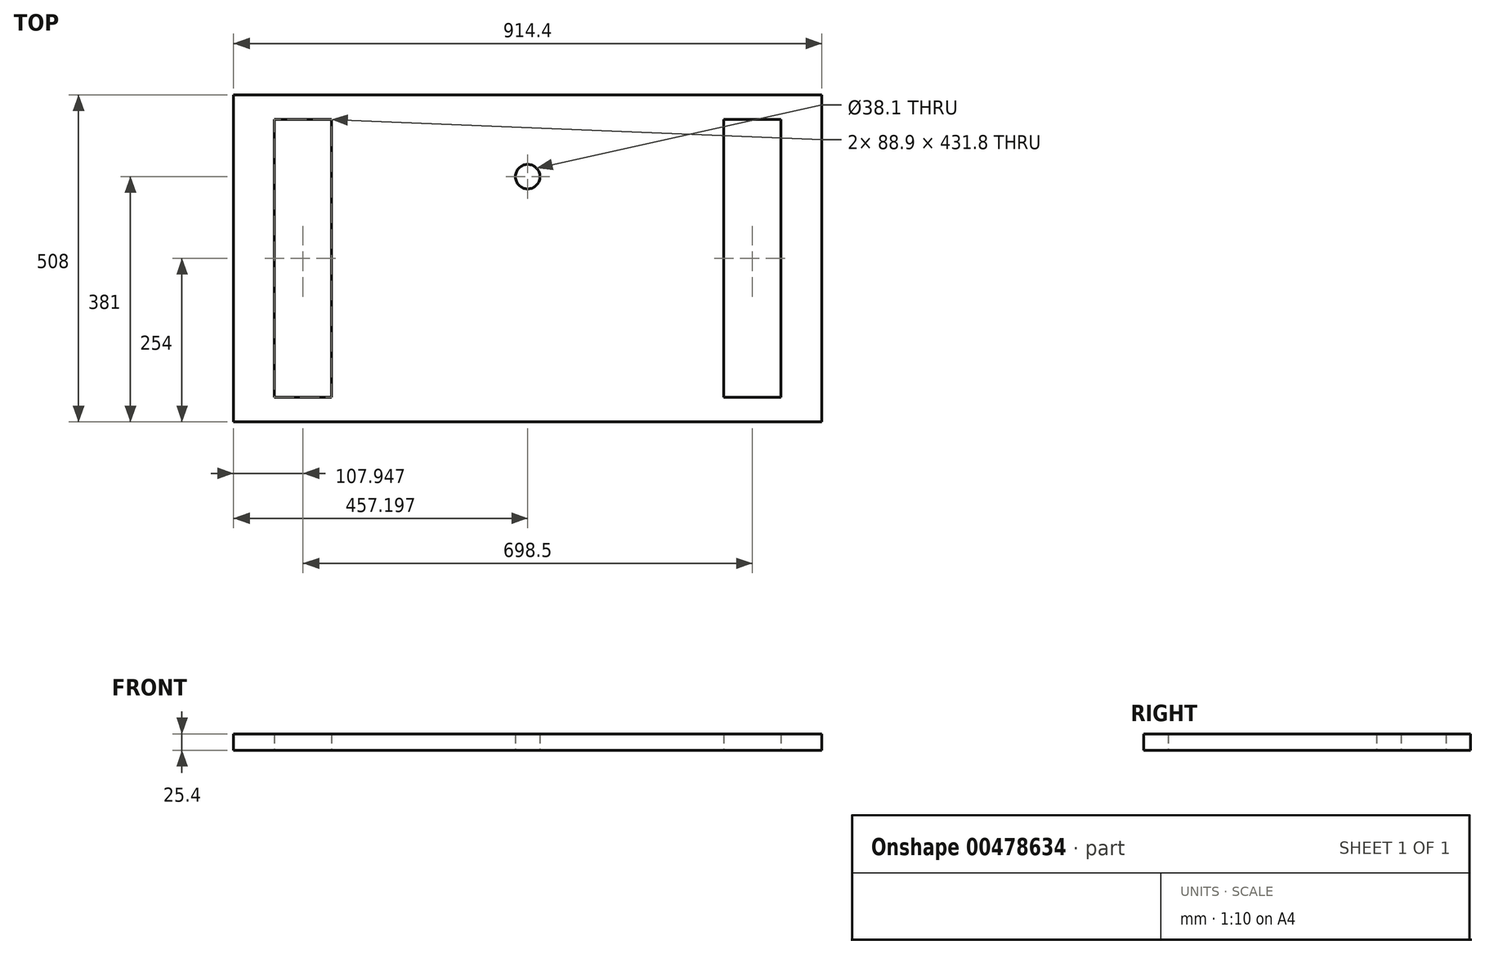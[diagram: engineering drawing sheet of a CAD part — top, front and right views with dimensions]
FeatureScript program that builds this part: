
annotation { "Feature Type Name" : "Feature", "Feature Type Description" : "" }
export const myFeature = defineFeature(function(context is Context, id is Id, definition is map)
    precondition{}
    {
        {
            var Q0;
            Q0=qCreatedBy(makeId("Top.planeOp"),FACE);
            var sketch = newSketch(context, id + "F0", { "sketchPlane" : qUnion([Q0])});
            skLineSegment(sketch, "E0.bottom", {"start": v(-444.73, 136.84) * mm, "end": v(469.67, 136.84) * mm});
            skLineSegment(sketch, "E0.top", {"start": v(-444.73, -371.16) * mm, "end": v(469.67, -371.16) * mm});
            skLineSegment(sketch, "E0.left", {"start": v(-444.73, 136.84) * mm, "end": v(-444.73, -371.16) * mm});
            skLineSegment(sketch, "E0.right", {"start": v(469.67, 136.84) * mm, "end": v(469.67, -371.16) * mm});
            skLineSegment(sketch, "E1", {"start": v(12.47, 136.84) * mm, "end": v(12.47, -371.16) * mm, "construction": true});
            skLineSegment(sketch, "E2.bottom", {"start": v(-381.23, 98.74) * mm, "end": v(-292.33, 98.74) * mm});
            skLineSegment(sketch, "E2.top", {"start": v(-381.23, -333.06) * mm, "end": v(-292.33, -333.06) * mm});
            skLineSegment(sketch, "E2.left", {"start": v(-381.23, 98.74) * mm, "end": v(-381.23, -333.06) * mm});
            skLineSegment(sketch, "E2.right", {"start": v(-292.33, 98.74) * mm, "end": v(-292.33, -333.06) * mm});
            skLineSegment(sketch, "E3", {"start": v(-292.33, -333.06) * mm, "end": v(-292.33, -371.16) * mm, "construction": true});
            skLineSegment(sketch, "E4", {"start": v(-381.23, -333.06) * mm, "end": v(-444.73, -333.06) * mm});
            skLineSegment(sketch, "E5.MirrorCS", {"start": v(406.17, -333.06) * mm, "end": v(317.27, -333.06) * mm});
            skLineSegment(sketch, "E6.MirrorCS", {"start": v(406.17, 98.74) * mm, "end": v(406.17, -333.06) * mm});
            skLineSegment(sketch, "E7.MirrorCS", {"start": v(317.27, 98.74) * mm, "end": v(317.27, -333.06) * mm});
            skLineSegment(sketch, "E8.MirrorCS", {"start": v(406.17, 98.74) * mm, "end": v(317.27, 98.74) * mm});
            skCircle(sketch, "E9", {"center": v(12.47, 9.84) * mm, "radius": 19.05 * mm});
            skSolve(sketch);
        }
        {
            var Q0;
            {var subQ0=sQuery(id+"F0.wireOp",EDGE,"E0.bottom");Q0=makeQuery(id+"F0.imprint","IMPRINT",FACE,{"disambiguationData":[TD([[makeQuery(id+"F0.imprint","IMPRINT",EDGE,{"derivedFrom":subQ0}),-1.0]])]});}
            extrude(context, id + "F1", {"entities" : qUnion([Q0]), "depth" : 25.4 * mm, "offsetDistance" : 25.4 * mm});
        }
    });
